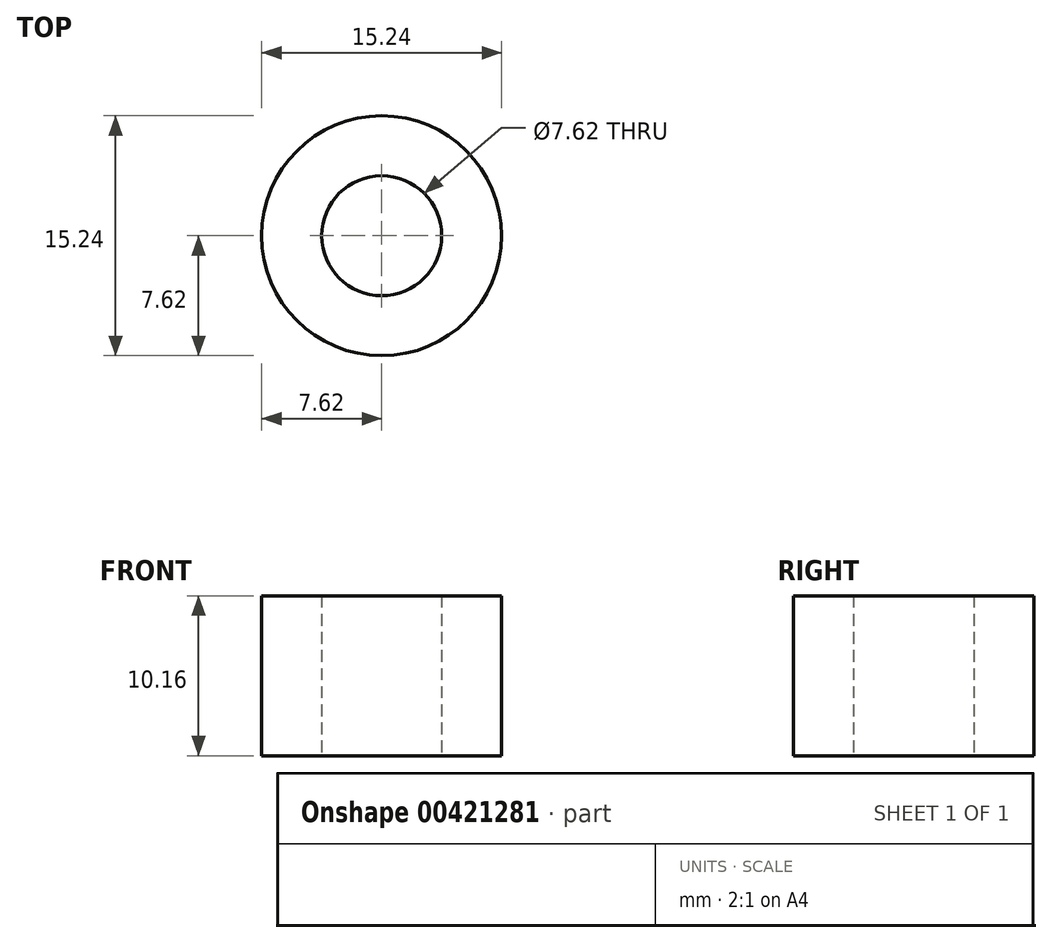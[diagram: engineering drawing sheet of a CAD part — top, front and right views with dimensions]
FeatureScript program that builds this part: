
annotation { "Feature Type Name" : "Feature", "Feature Type Description" : "" }
export const myFeature = defineFeature(function(context is Context, id is Id, definition is map)
    precondition{}
    {
        {
            var Q0;
            Q0=qCreatedBy(makeId("Top.planeOp"),FACE);
            var sketch = newSketch(context, id + "F0", { "sketchPlane" : qUnion([Q0])});
            skCircle(sketch, "E0", {"center": v(0, 0) * mm, "radius": 3.81 * mm});
            skCircle(sketch, "E1", {"center": v(0, 0) * mm, "radius": 7.62 * mm});
            skSolve(sketch);
        }
        {
            var Q0;
            Q0 = qSketchRegion(id + "F0", true);
            extrude(context, id + "F1", {"entities" : qUnion([Q0]), "depth" : 10.16 * mm, "offsetDistance" : 25.4 * mm});
        }
    });
